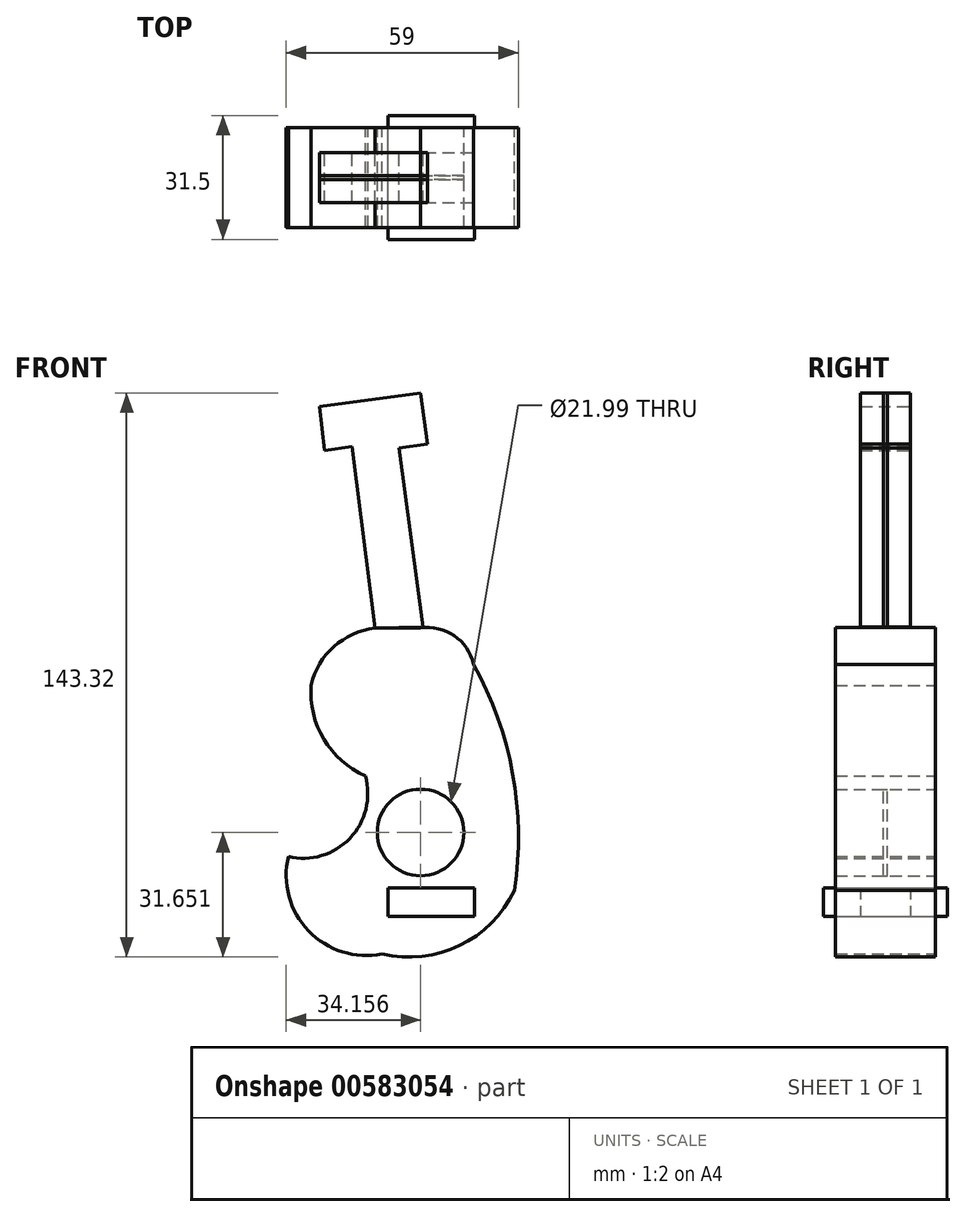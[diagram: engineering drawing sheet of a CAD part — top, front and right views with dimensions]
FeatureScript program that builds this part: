
annotation { "Feature Type Name" : "Feature", "Feature Type Description" : "" }
export const myFeature = defineFeature(function(context is Context, id is Id, definition is map)
    precondition{}
    {
        {
            var Q0;
            Q0=qCreatedBy(makeId("Front.planeOp"),FACE);
            var sketch = newSketch(context, id + "F0", { "sketchPlane" : qUnion([Q0])});
            skArc(sketch, "E0", {"start": v(-70.7, -43.52) * mm, "mid": v(-65.56, -62.4) * mm, "end": v(-46.88, -68.25) * mm});
            skArc(sketch, "E1", {"start": v(-46.88, -68.25) * mm, "mid": v(-27.2, -66.14) * mm, "end": v(-13.28, -52.07) * mm});
            skArc(sketch, "E2", {"start": v(-70.7, -43.52) * mm, "mid": v(-55.06, -38.89) * mm, "end": v(-51.15, -23.06) * mm});
            skArc(sketch, "E3", {"start": v(-64.9, 0) * mm, "mid": v(-61.68, -13.7) * mm, "end": v(-51.15, -23.06) * mm});
            skArc(sketch, "E4", {"start": v(-13.28, -52.07) * mm, "mid": v(-13.7, -22.5) * mm, "end": v(-23.67, 5.34) * mm});
            skArc(sketch, "E5", {"start": v(-48.7, 14.5) * mm, "mid": v(-59.1, 9.83) * mm, "end": v(-64.9, 0) * mm});
            skArc(sketch, "E6", {"start": v(-23.67, 5.34) * mm, "mid": v(-28.56, 12.6) * mm, "end": v(-37.1, 14.5) * mm});
            skCircle(sketch, "E7", {"center": v(-37.1, -37.4) * mm, "radius": 11 * mm});
            skLineSegment(sketch, "E8", {"start": v(-37.1, 14.5) * mm, "end": v(-48.7, 14.5) * mm});
            skSolve(sketch);
        }
        {
            var Q0;
            Q0=qCreatedBy(makeId("Front.planeOp"),FACE);
            var sketch = newSketch(context, id + "F1", { "sketchPlane" : qUnion([Q0])});
            skLineSegment(sketch, "E9", {"start": v(-48.7, 14.5) * mm, "end": v(-54.51, 60.62) * mm});
            skLineSegment(sketch, "E10", {"start": v(-36.5, 14.81) * mm, "end": v(-42.6, 60.31) * mm});
            skLineSegment(sketch, "E11", {"start": v(-54.51, 60.62) * mm, "end": v(-61.45, 59.69) * mm});
            skLineSegment(sketch, "E12", {"start": v(-42.6, 60.31) * mm, "end": v(-35.36, 61.28) * mm});
            skLineSegment(sketch, "E13", {"start": v(-35.36, 61.28) * mm, "end": v(-37.1, 74.26) * mm});
            skLineSegment(sketch, "E14", {"start": v(-37.1, 74.26) * mm, "end": v(-62.75, 70.82) * mm});
            skLineSegment(sketch, "E15", {"start": v(-62.75, 70.82) * mm, "end": v(-61.45, 59.69) * mm});
            skLineSegment(sketch, "E16", {"start": v(-42.6, 60.31) * mm, "end": v(-54.51, 60.62) * mm});
            skLineSegment(sketch, "E17", {"start": v(-36.5, 14.81) * mm, "end": v(-48.7, 14.5) * mm});
            skSolve(sketch);
        }
        {
            var Q0;
            Q0=qCreatedBy(makeId("Front.planeOp"),FACE);
            var sketch = newSketch(context, id + "F2", { "sketchPlane" : qUnion([Q0])});
            skLineSegment(sketch, "E18", {"start": v(-54.2, 67.64) * mm, "end": v(-38.94, -53.6) * mm});
            skLineSegment(sketch, "E19", {"start": v(-51.46, 67.64) * mm, "end": v(-36.2, -53.48) * mm});
            skLineSegment(sketch, "E20", {"start": v(-48.4, 67.64) * mm, "end": v(-33.15, -53.45) * mm});
            skLineSegment(sketch, "E21", {"start": v(-45.35, 67.64) * mm, "end": v(-30.1, -53.45) * mm});
            skLineSegment(sketch, "E22.bottom", {"start": v(-45.35, -51.46) * mm, "end": v(-23.36, -51.46) * mm});
            skLineSegment(sketch, "E22.top", {"start": v(-45.35, -58.79) * mm, "end": v(-23.36, -58.79) * mm});
            skLineSegment(sketch, "E22.left", {"start": v(-45.35, -51.46) * mm, "end": v(-45.35, -58.79) * mm});
            skLineSegment(sketch, "E22.right", {"start": v(-23.36, -51.46) * mm, "end": v(-23.36, -58.79) * mm});
            skSolve(sketch);
        }
        {
            var Q0;
            Q0 = qSketchRegion(id + "F2", true);
            var Q1;
            Q1 = qSketchRegion(id + "F1", true);
            extrude(context, id + "F3", {"entities" : qUnion([Q0, Q1]), "endBound" : BoundingType.SYMMETRIC, "depth" : 12.7 * mm, "offsetDistance" : 25.4 * mm});
        }
        {
            var Q0;
            Q0 = qSketchRegion(id + "F1", true);
            var Q1;
            Q1=makeQuery(id+"F0.imprint","IMPRINT",FACE,{"disambiguationData":[TD([[makeQuery(id+"F0.imprint","IMPRINT",EDGE,{"derivedFrom":sQuery(id+"F0.wireOp",EDGE,"E7")}),1.0]])]});
            extrude(context, id + "F4", {"entities" : qUnion([Q0, Q1]), "endBound" : BoundingType.SYMMETRIC, "depth" : 1.02 * mm, "offsetDistance" : 25.4 * mm});
        }
        {
            var Q0;
            Q0 = qSketchRegion(id + "F0", true);
            extrude(context, id + "F5", {"entities" : qUnion([Q0]), "endBound" : BoundingType.SYMMETRIC, "depth" : 25.4 * mm, "offsetDistance" : 25.4 * mm});
        }
        {
            var Q0;
            Q0 = qSketchRegion(id + "F2", true);
            extrude(context, id + "F6", {"entities" : qUnion([Q0]), "endBound" : BoundingType.SYMMETRIC, "depth" : 31.5 * mm, "offsetDistance" : 25.4 * mm});
        }
    });
